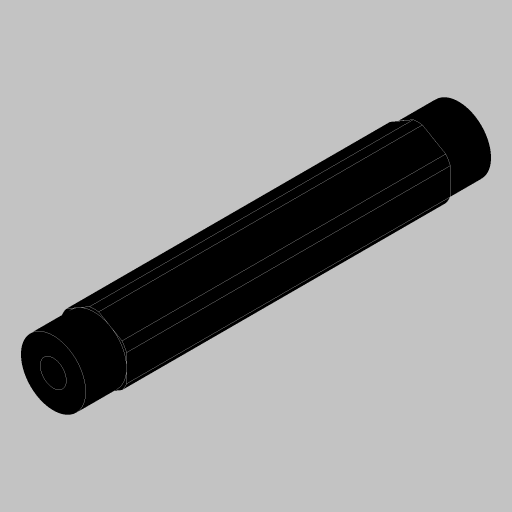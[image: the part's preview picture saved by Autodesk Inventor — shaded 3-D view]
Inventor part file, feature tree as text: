
AUTODESK INVENTOR PART (.ipt)
format: ipt  version: 2023.5 (Build 275446000, 446)  size: 163,328 bytes
history: native  units: in
note: dims shown in document units (in); Inventor stores cm internally (conversion verified against a paired STEP export)
features: extrude x3, projected_geometry x3, hole x1, mirror x1, sketch x1
ambient origin geometry x8: Origin, YZ Plane, XZ Plane, XY Plane, X Axis, Y Axis, Z Axis, Center Point
bodies: Solid1 (feature_tree)
feature tree (9):
  extrude  "Extrusion1"  Depth=0.315in
  hole  "Hole1"  [1 undecoded]
  extrude  "Extrusion3"  Depth=0.5in
  extrude  "Extrusion4"  Depth=0.315in TaperAngle=0.0deg
  mirror  "Mirror2"
  sketch  "Sketch5"  dims[d2=0.0in d9=0.625in d10=0.385in d11=0.25in d12=0.5635in d13=1.0in d14=0.8108in d16=0.7in d17=0.0in d18=0.0in d19=0.5in d20=0.315in d21=0.0in]
  projected_geometry  "Project Cut Edges1"
  projected_geometry  "Project Cut Edges2"
  projected_geometry  "Project Cut Edges3"
note: 1 required parameter value undecoded (feature->parameter linkage not recoverable at this tier; creation-order binding heuristic only, values carry confidence <= 0.55)
